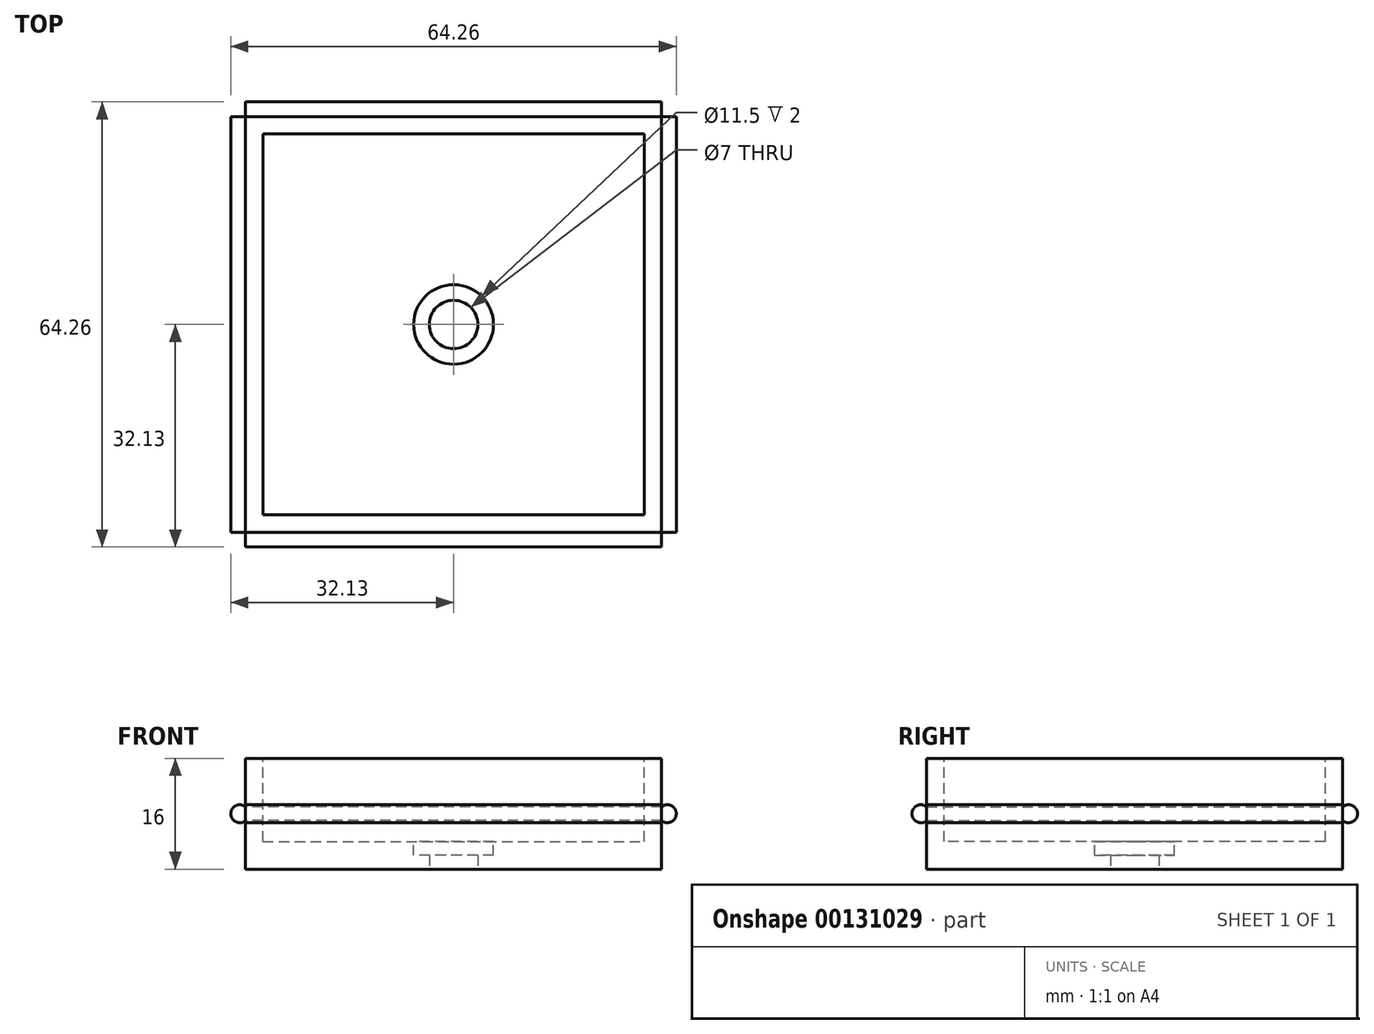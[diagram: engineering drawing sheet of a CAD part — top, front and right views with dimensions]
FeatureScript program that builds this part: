
annotation { "Feature Type Name" : "Feature", "Feature Type Description" : "" }
export const myFeature = defineFeature(function(context is Context, id is Id, definition is map)
    precondition{}
    {
        {
            var Q0;
            Q0=qCreatedBy(makeId("Top.planeOp"),FACE);
            var sketch = newSketch(context, id + "F0", { "sketchPlane" : qUnion([Q0])});
            skLineSegment(sketch, "E0.bottom", {"start": v(-30, 30) * mm, "end": v(30, 30) * mm});
            skLineSegment(sketch, "E0.top", {"start": v(-30, -30) * mm, "end": v(30, -30) * mm});
            skLineSegment(sketch, "E0.left", {"start": v(-30, 30) * mm, "end": v(-30, -30) * mm});
            skLineSegment(sketch, "E0.right", {"start": v(30, 30) * mm, "end": v(30, -30) * mm});
            skPoint(sketch, "E0.middle", {"position": v(0, 0) * mm});
            skCircle(sketch, "E1", {"center": v(0, 0) * mm, "radius": 3.5 * mm});
            skSolve(sketch);
        }
        {
            var Q0;
            Q0 = qSketchRegion(id + "F0", true);
            extrude(context, id + "F1", {"entities" : qUnion([Q0]), "depth" : 8 * mm, "hasSecondDirection" : true, "secondDirectionOppositeDirection" : true, "secondDirectionDepth" : 8 * mm});
        }
        {
            var Q0;
            Q0=makeQuery(id+"F1.opExtrude","CAP_FACE",FACE,{"disambiguationData":[OSD([sQuery(id+"F0.wireOp",EDGE,"E0.bottom"),sQuery(id+"F0.wireOp",EDGE,"E0.top"),sQuery(id+"F0.wireOp",EDGE,"E0.left"),sQuery(id+"F0.wireOp",EDGE,"E0.right"),sQuery(id+"F0.wireOp",EDGE,"E1")])],"isStart":false});
            var sketch = newSketch(context, id + "F2", { "sketchPlane" : qUnion([Q0])});
            skCircle(sketch, "E2", {"center": v(0, 0) * mm, "radius": 5.75 * mm});
            skSolve(sketch);
        }
        {
            var Q0;
            Q0 = qSketchRegion(id + "F2", true);
            extrude(context, id + "F3", {"entities" : qUnion([Q0]), "operationType" : NewBodyOperationType.REMOVE, "oppositeDirection" : true, "depth" : 14 * mm});
        }
        {
            var Q0;
            Q0=makeQuery(id+"F1.opExtrude","SWEPT_FACE",FACE,{"disambiguationData":[OSD([sQuery(id+"F0.wireOp",EDGE,"E0.left")])]});
            var sketch = newSketch(context, id + "F4", { "sketchPlane" : qUnion([Q0])});
            skLineSegment(sketch, "E3", {"start": v(-30, 0) * mm, "end": v(-25.83, 0) * mm, "construction": true});
            skLineSegment(sketch, "E4", {"start": v(-30, -1) * mm, "end": v(-30, 1) * mm});
            skArc(sketch, "E5", {"start": v(-30, 1) * mm, "mid": v(-32.13, 0) * mm, "end": v(-30, -1) * mm});
            skSolve(sketch);
        }
        {
            var Q0;
            Q0=makeQuery(id+"F4.imprint","IMPRINT",FACE,{"disambiguationData":[TD([[makeQuery(id+"F4.imprint","IMPRINT",EDGE,{"derivedFrom":sQuery(id+"F4.wireOp",EDGE,"E4")}),-1.0]])]});
            extrude(context, id + "F5", {"entities" : qUnion([Q0]), "oppositeDirection" : true, "depth" : 60 * mm});
        }
        {
            var Q0;
            Q0=makeQuery(id+"F5.opExtrude","SWEPT_BODY",BODY,{"disambiguationData":[OSD([sQuery(id+"F4.wireOp",EDGE,"E4"),sQuery(id+"F4.wireOp",EDGE,"E5")])]});
            var Q1;
            Q1=qCreatedBy(makeId("Front.planeOp"),FACE);
            mirror(context, id + "F6", {"operationType" : NewBodyOperationType.ADD, "entities" : qUnion([Q0]), "mirrorPlane" : qUnion([Q1])});
        }
        {
            var Q0;
            {var subQ3=sQuery(id+"F0.wireOp",EDGE,"E0.right");var subQ4=sQuery(id+"F0.wireOp",EDGE,"E0.left");var subQ6=sQuery(id+"F0.wireOp",EDGE,"E0.bottom");Q0=makeQuery(id+"F6.boolean.opBoolean","SPLIT",FACE,{"disambiguationData":[TD([makeQuery(id+"F1.opExtrude","CAP_FACE",FACE,{"disambiguationData":[OSD([subQ6,sQuery(id+"F0.wireOp",EDGE,"E0.top"),subQ4,subQ3,sQuery(id+"F0.wireOp",EDGE,"E1")])],"isStart":true})])],"derivedFrom":makeQuery(id+"F1.opExtrude","SWEPT_FACE",FACE,{"disambiguationData":[OSD([subQ6])]})});}
            var sketch = newSketch(context, id + "F7", { "sketchPlane" : qUnion([Q0])});
            skLineSegment(sketch, "E6", {"start": v(30, 1) * mm, "end": v(30, -1) * mm});
            skArc(sketch, "E7", {"start": v(30, -1) * mm, "mid": v(32.13, 0) * mm, "end": v(30, 1) * mm});
            skSolve(sketch);
        }
        {
            var Q0;
            Q0 = qSketchRegion(id + "F7", true);
            extrude(context, id + "F8", {"entities" : qUnion([Q0]), "oppositeDirection" : true, "depth" : 60 * mm});
        }
        {
            var Q0;
            Q0=makeQuery(id+"F8.opExtrude","SWEPT_BODY",BODY,{"disambiguationData":[OSD([sQuery(id+"F7.wireOp",EDGE,"E6"),sQuery(id+"F7.wireOp",EDGE,"E7")])]});
            var Q1;
            Q1=qCreatedBy(makeId("Right.planeOp"),FACE);
            mirror(context, id + "F9", {"operationType" : NewBodyOperationType.ADD, "entities" : qUnion([Q0]), "mirrorPlane" : qUnion([Q1])});
        }
        {
            var Q0;
            Q0=makeQuery(id+"F1.opExtrude","CAP_FACE",FACE,{"disambiguationData":[OSD([sQuery(id+"F0.wireOp",EDGE,"E0.bottom"),sQuery(id+"F0.wireOp",EDGE,"E0.top"),sQuery(id+"F0.wireOp",EDGE,"E0.left"),sQuery(id+"F0.wireOp",EDGE,"E0.right"),sQuery(id+"F0.wireOp",EDGE,"E1")])],"isStart":false});
            var sketch = newSketch(context, id + "F10", { "sketchPlane" : qUnion([Q0])});
            skLineSegment(sketch, "E8.bottom", {"start": v(-27.5, 27.5) * mm, "end": v(27.5, 27.5) * mm});
            skLineSegment(sketch, "E8.top", {"start": v(-27.5, -27.5) * mm, "end": v(27.5, -27.5) * mm});
            skLineSegment(sketch, "E8.left", {"start": v(-27.5, 27.5) * mm, "end": v(-27.5, -27.5) * mm});
            skLineSegment(sketch, "E8.right", {"start": v(27.5, 27.5) * mm, "end": v(27.5, -27.5) * mm});
            skPoint(sketch, "E8.middle", {"position": v(0, 0) * mm});
            skSolve(sketch);
        }
        {
            var Q0;
            Q0 = qSketchRegion(id + "F10", true);
            extrude(context, id + "F11", {"entities" : qUnion([Q0]), "operationType" : NewBodyOperationType.REMOVE, "oppositeDirection" : true, "depth" : 12 * mm});
        }
    });
